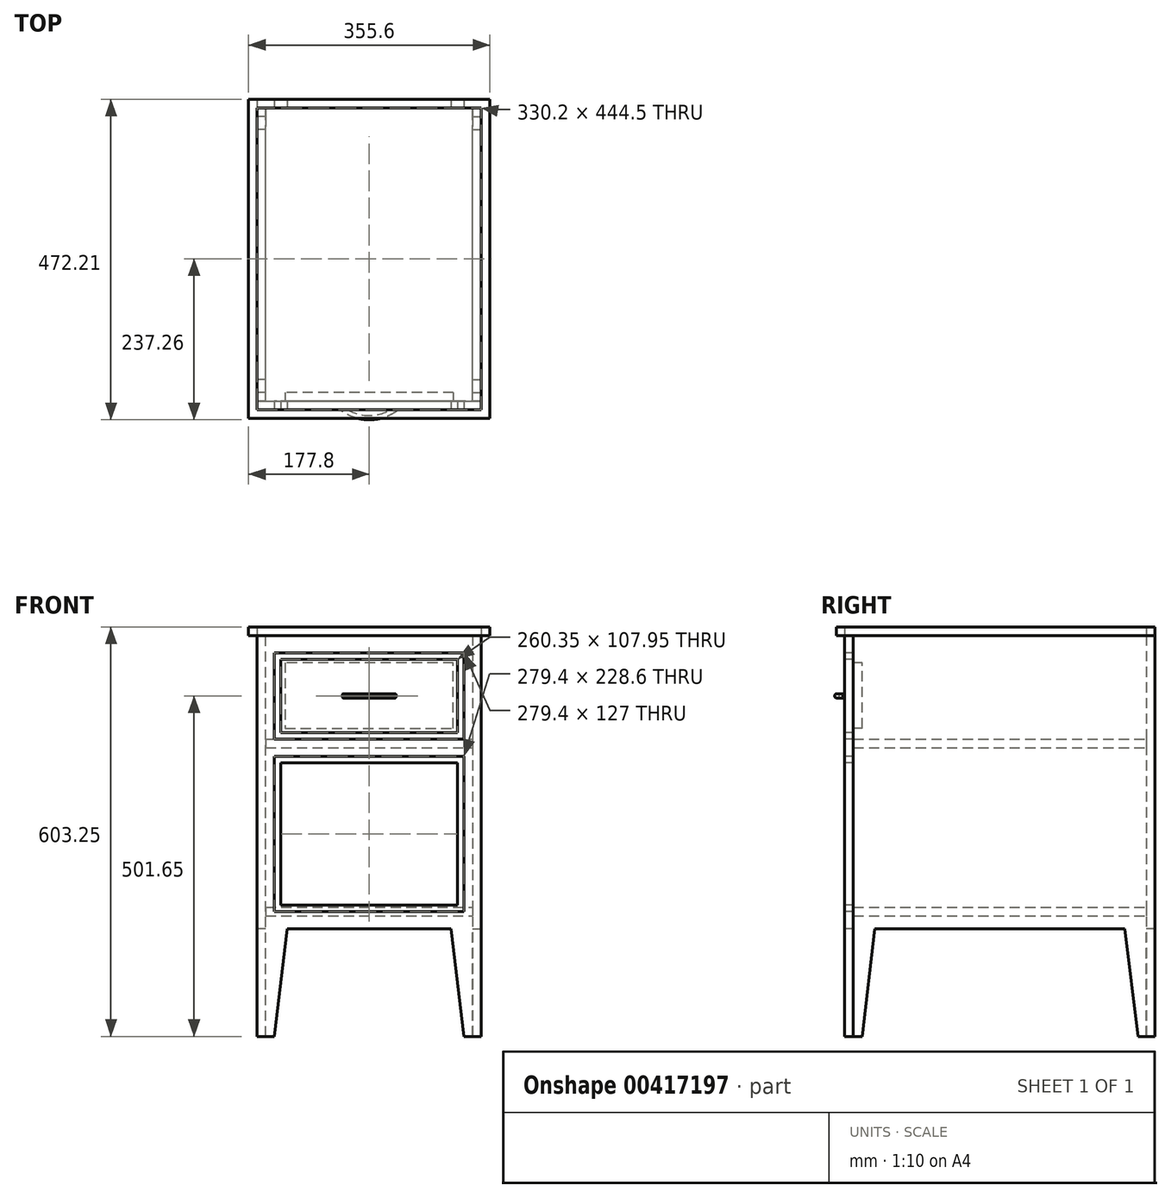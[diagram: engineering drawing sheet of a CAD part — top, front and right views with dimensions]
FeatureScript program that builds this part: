
annotation { "Feature Type Name" : "Feature", "Feature Type Description" : "" }
export const myFeature = defineFeature(function(context is Context, id is Id, definition is map)
    precondition{}
    {
        {
            var Q0;
            Q0=qCreatedBy(makeId("Front.planeOp"),FACE);
            var sketch = newSketch(context, id + "F0", { "sketchPlane" : qUnion([Q0])});
            skLineSegment(sketch, "E0.bottom", {"start": v(44.45, 0) * mm, "end": v(285.75, 0) * mm});
            skLineSegment(sketch, "E0.top", {"start": v(0, 431.8) * mm, "end": v(330.2, 431.8) * mm});
            skLineSegment(sketch, "E0.left", {"start": v(0, 0) * mm, "end": v(0, 431.8) * mm});
            skLineSegment(sketch, "E0.right", {"start": v(330.2, 0) * mm, "end": v(330.2, 431.8) * mm});
            skLineSegment(sketch, "E1", {"start": v(0, 0) * mm, "end": v(0, -158.75) * mm});
            skLineSegment(sketch, "E2", {"start": v(25.4, -158.75) * mm, "end": v(44.45, 0) * mm});
            skLineSegment(sketch, "E3", {"start": v(0, -158.75) * mm, "end": v(25.4, -158.75) * mm});
            skLineSegment(sketch, "E4", {"start": v(165.1, 431.8) * mm, "end": v(165.1, -6.98) * mm, "construction": true});
            skLineSegment(sketch, "E5.MirrorCS", {"start": v(304.8, -158.75) * mm, "end": v(285.75, 0) * mm});
            skLineSegment(sketch, "E6.MirrorCS", {"start": v(330.2, -158.75) * mm, "end": v(304.8, -158.75) * mm});
            skLineSegment(sketch, "E7.MirrorCS", {"start": v(330.2, 0) * mm, "end": v(330.2, -158.75) * mm});
            skLineSegment(sketch, "E8.bottom", {"start": v(304.8, 279.4) * mm, "end": v(25.4, 279.4) * mm});
            skLineSegment(sketch, "E8.top", {"start": v(304.8, 406.4) * mm, "end": v(25.4, 406.4) * mm});
            skLineSegment(sketch, "E8.left", {"start": v(304.8, 279.4) * mm, "end": v(304.8, 406.4) * mm});
            skLineSegment(sketch, "E8.right", {"start": v(25.4, 279.4) * mm, "end": v(25.4, 406.4) * mm});
            skPoint(sketch, "E8.middle", {"position": v(165.1, 342.9) * mm});
            skLineSegment(sketch, "E9.bottom", {"start": v(304.8, 25.4) * mm, "end": v(25.4, 25.4) * mm});
            skLineSegment(sketch, "E9.top", {"start": v(304.8, 254) * mm, "end": v(25.4, 254) * mm});
            skLineSegment(sketch, "E9.left", {"start": v(304.8, 25.4) * mm, "end": v(304.8, 254) * mm});
            skLineSegment(sketch, "E9.right", {"start": v(25.4, 25.4) * mm, "end": v(25.4, 254) * mm});
            skPoint(sketch, "E9.middle", {"position": v(165.1, 139.7) * mm});
            skSolve(sketch);
        }
        {
            var Q0;
            Q0=makeQuery(id+"F0.imprint","IMPRINT",FACE,{"disambiguationData":[TD([[makeQuery(id+"F0.imprint","IMPRINT",EDGE,{"derivedFrom":sQuery(id+"F0.wireOp",EDGE,"E0.bottom")}),1.0]])]});
            extrude(context, id + "F1", {"entities" : qUnion([Q0]), "oppositeDirection" : true, "depth" : 12.7 * mm});
        }
        {
            var Q0;
            Q0=makeQuery(id+"F1.opExtrude","SWEPT_FACE",FACE,{"disambiguationData":[OSD([sQuery(id+"F0.wireOp",EDGE,"E0.right"),sQuery(id+"F0.wireOp",EDGE,"E7.MirrorCS")])]});
            var sketch = newSketch(context, id + "F2", { "sketchPlane" : qUnion([Q0])});
            skLineSegment(sketch, "E10.0", {"start": v(12.7, 431.8) * mm, "end": v(12.7, -158.75) * mm});
            skLineSegment(sketch, "E11.top", {"start": v(12.7, 431.8) * mm, "end": v(444.5, 431.8) * mm});
            skLineSegment(sketch, "E12", {"start": v(25.4, -158.75) * mm, "end": v(44.45, 0) * mm});
            skLineSegment(sketch, "E13", {"start": v(12.7, -158.75) * mm, "end": v(25.4, -158.75) * mm});
            skLineSegment(sketch, "E14.MirrorCS", {"start": v(431.8, -158.75) * mm, "end": v(412.75, 0) * mm});
            skLineSegment(sketch, "E15.MirrorCS", {"start": v(444.5, -158.75) * mm, "end": v(431.8, -158.75) * mm});
            skLineSegment(sketch, "E16.MirrorCS", {"start": v(444.5, 431.8) * mm, "end": v(444.5, -158.75) * mm});
            skPoint(sketch, "E17.middle", {"position": v(184.15, 419.1) * mm});
            skPoint(sketch, "E18.middle", {"position": v(184.15, 177.8) * mm});
            skLineSegment(sketch, "E19", {"start": v(44.45, 0) * mm, "end": v(412.75, 0) * mm});
            skSolve(sketch);
        }
        {
            var Q0;
            Q0=makeQuery(id+"F2.imprint","IMPRINT",FACE,{"disambiguationData":[TD([[makeQuery(id+"F2.imprint","IMPRINT",EDGE,{"derivedFrom":sQuery(id+"F2.wireOp",EDGE,"E11.top")}),-1.0]])]});
            extrude(context, id + "F3", {"entities" : qUnion([Q0]), "oppositeDirection" : true, "depth" : 12.7 * mm});
        }
        {
            var Q0;
            Q0=makeQuery(id+"F3.opExtrude","SWEPT_FACE",FACE,{"disambiguationData":[OSD([sQuery(id+"F2.wireOp",EDGE,"E16.MirrorCS")])]});
            var sketch = newSketch(context, id + "F4", { "sketchPlane" : qUnion([Q0])});
            skLineSegment(sketch, "E20.bottom", {"start": v(-285.75, 0) * mm, "end": v(-44.45, 0) * mm});
            skLineSegment(sketch, "E20.top", {"start": v(-330.2, 431.8) * mm, "end": v(0, 431.8) * mm});
            skLineSegment(sketch, "E20.left", {"start": v(-330.2, 0) * mm, "end": v(-330.2, 431.8) * mm});
            skLineSegment(sketch, "E20.right", {"start": v(0, 0) * mm, "end": v(0, 431.8) * mm});
            skLineSegment(sketch, "E21", {"start": v(-330.2, 0) * mm, "end": v(-330.2, -158.75) * mm});
            skLineSegment(sketch, "E22", {"start": v(-304.8, -158.75) * mm, "end": v(-285.75, 0) * mm});
            skLineSegment(sketch, "E23", {"start": v(-330.2, -158.75) * mm, "end": v(-304.8, -158.75) * mm});
            skLineSegment(sketch, "E24", {"start": v(-165.1, 431.8) * mm, "end": v(-165.1, 33.68) * mm, "construction": true});
            skLineSegment(sketch, "E25.MirrorCS", {"start": v(-25.4, -158.75) * mm, "end": v(-44.45, 0) * mm});
            skLineSegment(sketch, "E26.MirrorCS", {"start": v(0, -158.75) * mm, "end": v(-25.4, -158.75) * mm});
            skLineSegment(sketch, "E27.MirrorCS", {"start": v(0, 0) * mm, "end": v(0, -158.75) * mm});
            skPoint(sketch, "E28.middle", {"position": v(-165.1, 419.1) * mm});
            skPoint(sketch, "E29.middle", {"position": v(-165.1, 177.8) * mm});
            skSolve(sketch);
        }
        {
            var Q0;
            Q0=qSketchRegion(id+"F4",true);
            extrude(context, id + "F5", {"entities" : qUnion([Q0]), "operationType" : NewBodyOperationType.ADD, "depth" : 12.7 * mm});
        }
        {
            var Q0;
            Q0=qCreatedBy(makeId("Right.planeOp"),FACE);
            var sketch = newSketch(context, id + "F6", { "sketchPlane" : qUnion([Q0])});
            skLineSegment(sketch, "E30.0", {"start": v(25.4, -158.75) * mm, "end": v(44.45, 0) * mm});
            skLineSegment(sketch, "E31.0", {"start": v(44.45, 0) * mm, "end": v(412.75, 0) * mm});
            skLineSegment(sketch, "E32.0", {"start": v(431.8, -158.75) * mm, "end": v(412.75, 0) * mm});
            skLineSegment(sketch, "E33.0", {"start": v(12.7, -158.75) * mm, "end": v(12.7, 431.8) * mm});
            skLineSegment(sketch, "E34.0", {"start": v(444.5, 431.8) * mm, "end": v(444.5, -158.75) * mm});
            skLineSegment(sketch, "E35.0", {"start": v(12.7, 431.8) * mm, "end": v(444.5, 431.8) * mm});
            skLineSegment(sketch, "E36.0", {"start": v(12.7, -158.75) * mm, "end": v(25.4, -158.75) * mm});
            skLineSegment(sketch, "E37.0", {"start": v(444.5, -158.75) * mm, "end": v(431.8, -158.75) * mm});
            skSolve(sketch);
        }
        {
            var Q0;
            Q0=qSketchRegion(id+"F6",true);
            extrude(context, id + "F7", {"entities" : qUnion([Q0]), "depth" : 12.7 * mm});
        }
        {
            var Q0;
            Q0=makeQuery(id+"F7.boolean.opBoolean","MERGE",FACE,{"derivedFrom":[makeQuery(id+"F5.boolean.opBoolean","MERGE",FACE,{"derivedFrom":[makeQuery(id+"F3.boolean.opBoolean","MERGE",FACE,{"derivedFrom":[makeQuery(id+"F1.opExtrude","SWEPT_FACE",FACE,{"disambiguationData":[OSD([sQuery(id+"F0.wireOp",EDGE,"E0.top")])]}),makeQuery(id+"F3.opExtrude","SWEPT_FACE",FACE,{"disambiguationData":[OSD([sQuery(id+"F2.wireOp",EDGE,"E11.top")])]})]}),makeQuery(id+"F5.opExtrude","SWEPT_FACE",FACE,{"disambiguationData":[OSD([sQuery(id+"F4.wireOp",EDGE,"E20.top")])]})]}),makeQuery(id+"F7.opExtrude","SWEPT_FACE",FACE,{"disambiguationData":[OSD([sQuery(id+"F6.wireOp",EDGE,"E35.0")])]})]});
            var sketch = newSketch(context, id + "F8", { "sketchPlane" : qUnion([Q0])});
            skLineSegment(sketch, "E38", {"start": v(165.1, 12.7) * mm, "end": v(165.1, 444.5) * mm, "construction": true});
            skLineSegment(sketch, "E39.top", {"start": v(330.2, 0) * mm, "end": v(0, 0) * mm});
            skLineSegment(sketch, "E39.left", {"start": v(330.2, 444.5) * mm, "end": v(330.2, 0) * mm});
            skLineSegment(sketch, "E39.right", {"start": v(0, 444.5) * mm, "end": v(0, 0) * mm});
            skPoint(sketch, "E40", {"position": v(165.1, 228.6) * mm});
            skLineSegment(sketch, "E41", {"start": v(0, 444.5) * mm, "end": v(330.2, 444.5) * mm});
            skSolve(sketch);
        }
        {
            var Q0;
            Q0=qSketchRegion(id+"F8",true);
            extrude(context, id + "F9", {"entities" : qUnion([Q0]), "depth" : 12.7 * mm});
        }
        {
            var Q0;
            Q0=makeQuery(id+"F0.imprint","IMPRINT",FACE,{"disambiguationData":[TD([[makeQuery(id+"F0.imprint","IMPRINT",EDGE,{"derivedFrom":sQuery(id+"F0.wireOp",EDGE,"E0.bottom")}),1.0]])]});
            var sketch = newSketch(context, id + "F10", { "sketchPlane" : qUnion([Q0])});
            skLineSegment(sketch, "E42.0.0", {"start": v(304.8, 279.4) * mm, "end": v(304.8, 406.4) * mm});
            skLineSegment(sketch, "E42.0.1", {"start": v(304.8, 406.4) * mm, "end": v(25.4, 406.4) * mm});
            skLineSegment(sketch, "E42.0.2", {"start": v(25.4, 406.4) * mm, "end": v(25.4, 279.4) * mm});
            skLineSegment(sketch, "E42.0.3", {"start": v(25.4, 279.4) * mm, "end": v(304.8, 279.4) * mm});
            skLineSegment(sketch, "E43.0", {"start": v(34.93, 288.93) * mm, "end": v(295.28, 288.93) * mm});
            skLineSegment(sketch, "E43.1", {"start": v(34.93, 396.88) * mm, "end": v(34.93, 288.93) * mm});
            skLineSegment(sketch, "E43.2", {"start": v(295.28, 396.88) * mm, "end": v(34.93, 396.88) * mm});
            skLineSegment(sketch, "E43.3", {"start": v(295.28, 288.93) * mm, "end": v(295.28, 396.88) * mm});
            skSolve(sketch);
        }
        {
            var Q0;
            Q0=makeQuery(id+"F10.imprint","IMPRINT",FACE,{"disambiguationData":[TD([[makeQuery(id+"F10.imprint","IMPRINT",EDGE,{"derivedFrom":sQuery(id+"F10.wireOp",EDGE,"E43.0")}),1.0]])]});
            extrude(context, id + "F11", {"entities" : qUnion([Q0]), "oppositeDirection" : true, "depth" : 12.7 * mm});
        }
        {
            var Q0;
            Q0=makeQuery(id+"F7.opExtrude","SWEPT_FACE",FACE,{"disambiguationData":[OSD([sQuery(id+"F6.wireOp",EDGE,"E31.0")])]});
            var sketch = newSketch(context, id + "F12", { "sketchPlane" : qUnion([Q0])});
            skLineSegment(sketch, "E44.0", {"start": v(12.7, -12.7) * mm, "end": v(317.5, -12.7) * mm});
            skLineSegment(sketch, "E44.1", {"start": v(12.7, -12.7) * mm, "end": v(12.7, -444.5) * mm});
            skPoint(sketch, "E45.orphan", {"position": v(12.7, -44.45) * mm});
            skPoint(sketch, "E46.orphan", {"position": v(44.45, -12.7) * mm});
            skLineSegment(sketch, "E47.0", {"start": v(317.5, -12.7) * mm, "end": v(317.5, -444.5) * mm});
            skPoint(sketch, "E48.orphan", {"position": v(285.75, -12.7) * mm});
            skPoint(sketch, "E49.orphan", {"position": v(317.5, -44.45) * mm});
            skLineSegment(sketch, "E50.0", {"start": v(317.5, -444.5) * mm, "end": v(12.7, -444.5) * mm});
            skPoint(sketch, "E51.orphan", {"position": v(317.5, -412.75) * mm});
            skPoint(sketch, "E52.orphan", {"position": v(285.75, -444.5) * mm});
            skPoint(sketch, "E53.orphan", {"position": v(44.45, -444.5) * mm});
            skPoint(sketch, "E54.orphan", {"position": v(12.7, -412.75) * mm});
            skSolve(sketch);
        }
        {
            var Q0;
            Q0=qSketchRegion(id+"F12",true);
            extrude(context, id + "F13", {"entities" : qUnion([Q0]), "oppositeDirection" : true, "depth" : 12.7 * mm});
        }
        {
            var Q0;
            Q0=makeQuery(id+"F13.opExtrude","SWEPT_BODY",BODY,{"disambiguationData":[OSD([sQuery(id+"F12.wireOp",EDGE,"E44.0"),sQuery(id+"F12.wireOp",EDGE,"E44.1"),sQuery(id+"F12.wireOp",EDGE,"E47.0"),sQuery(id+"F12.wireOp",EDGE,"E50.0")])]});
            transform(context, id + "F14", {"entities" : qUnion([Q0]), "transformType" : TransformType.TRANSLATION_3D, "dx" : 0 * mm, "dy" : 0 * mm, "dz" : 12.7 * mm, "makeCopy" : true});
        }
        {
            var Q0;
            Q0=makeQuery(id+"F14.opPattern","COPY",BODY,{"derivedFrom":makeQuery(id+"F13.opExtrude","SWEPT_BODY",BODY,{"disambiguationData":[OSD([sQuery(id+"F12.wireOp",EDGE,"E44.0"),sQuery(id+"F12.wireOp",EDGE,"E44.1"),sQuery(id+"F12.wireOp",EDGE,"E47.0"),sQuery(id+"F12.wireOp",EDGE,"E50.0")])]}),"instanceName":"1"});
            transform(context, id + "F15", {"entities" : qUnion([Q0]), "transformType" : TransformType.TRANSLATION_3D, "dx" : 0 * mm, "dy" : 0 * mm, "dz" : 254 * mm, "makeCopy" : true});
        }
        {
            var Q0;
            Q0=makeQuery(id+"F11.opExtrude","CAP_FACE",FACE,{"disambiguationData":[OSD([sQuery(id+"F10.wireOp",EDGE,"E43.0"),sQuery(id+"F10.wireOp",EDGE,"E43.1"),sQuery(id+"F10.wireOp",EDGE,"E43.2"),sQuery(id+"F10.wireOp",EDGE,"E43.3")])],"isStart":false});
            var sketch = newSketch(context, id + "F16", { "sketchPlane" : qUnion([Q0])});
            skLineSegment(sketch, "E55.0", {"start": v(-288.93, 391.8) * mm, "end": v(-41.28, 391.8) * mm});
            skLineSegment(sketch, "E56.0", {"start": v(-288.93, 295.28) * mm, "end": v(-288.93, 391.8) * mm});
            skLineSegment(sketch, "E56.1", {"start": v(-41.28, 295.28) * mm, "end": v(-288.93, 295.28) * mm});
            skLineSegment(sketch, "E56.2", {"start": v(-41.28, 391.8) * mm, "end": v(-41.28, 295.28) * mm});
            skSolve(sketch);
        }
        {
            var Q0;
            Q0 = qSketchRegion(id + "F16", true);
            extrude(context, id + "F17", {"entities" : qUnion([Q0]), "depth" : 12.7 * mm});
        }
        {
            var Q0;
            Q0=makeQuery(id+"F13.opExtrude","SWEPT_BODY",BODY,{"disambiguationData":[OSD([sQuery(id+"F12.wireOp",EDGE,"E44.0"),sQuery(id+"F12.wireOp",EDGE,"E44.1"),sQuery(id+"F12.wireOp",EDGE,"E47.0"),sQuery(id+"F12.wireOp",EDGE,"E50.0")])]});
            deleteBodies(context, id + "F18", {"entities" : qUnion([Q0])});
        }
        {
            var Q0;
            Q0=makeQuery(id+"F1.opExtrude","CAP_FACE",FACE,{"disambiguationData":[OSD([sQuery(id+"F0.wireOp",EDGE,"E0.bottom"),sQuery(id+"F0.wireOp",EDGE,"E0.top"),sQuery(id+"F0.wireOp",EDGE,"E0.left"),sQuery(id+"F0.wireOp",EDGE,"E0.right"),sQuery(id+"F0.wireOp",EDGE,"E1"),sQuery(id+"F0.wireOp",EDGE,"E2"),sQuery(id+"F0.wireOp",EDGE,"E3"),sQuery(id+"F0.wireOp",EDGE,"E5.MirrorCS"),sQuery(id+"F0.wireOp",EDGE,"E6.MirrorCS"),sQuery(id+"F0.wireOp",EDGE,"E7.MirrorCS"),sQuery(id+"F0.wireOp",EDGE,"E8.bottom"),sQuery(id+"F0.wireOp",EDGE,"E8.top"),sQuery(id+"F0.wireOp",EDGE,"E8.left"),sQuery(id+"F0.wireOp",EDGE,"E8.right"),sQuery(id+"F0.wireOp",EDGE,"E9.bottom"),sQuery(id+"F0.wireOp",EDGE,"E9.top"),sQuery(id+"F0.wireOp",EDGE,"E9.left"),sQuery(id+"F0.wireOp",EDGE,"E9.right")])],"isStart":true});
            var sketch = newSketch(context, id + "F19", { "sketchPlane" : qUnion([Q0])});
            skLineSegment(sketch, "E57.0", {"start": v(25.4, 279.4) * mm, "end": v(25.4, 406.4) * mm});
            skLineSegment(sketch, "E57.1", {"start": v(304.8, 406.4) * mm, "end": v(25.4, 406.4) * mm});
            skLineSegment(sketch, "E57.2", {"start": v(304.8, 279.4) * mm, "end": v(304.8, 406.4) * mm});
            skLineSegment(sketch, "E57.3", {"start": v(304.8, 279.4) * mm, "end": v(25.4, 279.4) * mm});
            skLineSegment(sketch, "E58.0", {"start": v(295.28, 396.88) * mm, "end": v(34.93, 396.88) * mm});
            skLineSegment(sketch, "E58.1", {"start": v(295.28, 288.93) * mm, "end": v(295.28, 396.88) * mm});
            skLineSegment(sketch, "E58.2", {"start": v(295.28, 288.93) * mm, "end": v(34.93, 288.93) * mm});
            skLineSegment(sketch, "E58.3", {"start": v(34.93, 288.93) * mm, "end": v(34.93, 396.88) * mm});
            skSolve(sketch);
        }
        {
            var Q0;
            Q0 = qSketchRegion(id + "F19", true);
            extrude(context, id + "F20", {"entities" : qUnion([Q0]), "oppositeDirection" : true, "depth" : 12.7 * mm});
        }
        {
            var Q0;
            Q0=makeQuery(id+"F1.opExtrude","CAP_FACE",FACE,{"disambiguationData":[OSD([sQuery(id+"F0.wireOp",EDGE,"E0.bottom"),sQuery(id+"F0.wireOp",EDGE,"E0.top"),sQuery(id+"F0.wireOp",EDGE,"E0.left"),sQuery(id+"F0.wireOp",EDGE,"E0.right"),sQuery(id+"F0.wireOp",EDGE,"E1"),sQuery(id+"F0.wireOp",EDGE,"E2"),sQuery(id+"F0.wireOp",EDGE,"E3"),sQuery(id+"F0.wireOp",EDGE,"E5.MirrorCS"),sQuery(id+"F0.wireOp",EDGE,"E6.MirrorCS"),sQuery(id+"F0.wireOp",EDGE,"E7.MirrorCS"),sQuery(id+"F0.wireOp",EDGE,"E8.bottom"),sQuery(id+"F0.wireOp",EDGE,"E8.top"),sQuery(id+"F0.wireOp",EDGE,"E8.left"),sQuery(id+"F0.wireOp",EDGE,"E8.right"),sQuery(id+"F0.wireOp",EDGE,"E9.bottom"),sQuery(id+"F0.wireOp",EDGE,"E9.top"),sQuery(id+"F0.wireOp",EDGE,"E9.left"),sQuery(id+"F0.wireOp",EDGE,"E9.right")])],"isStart":true});
            var sketch = newSketch(context, id + "F21", { "sketchPlane" : qUnion([Q0])});
            skLineSegment(sketch, "E59.0", {"start": v(304.8, 254) * mm, "end": v(25.4, 254) * mm});
            skLineSegment(sketch, "E59.1", {"start": v(25.4, 25.4) * mm, "end": v(25.4, 254) * mm});
            skLineSegment(sketch, "E59.2", {"start": v(304.8, 25.4) * mm, "end": v(25.4, 25.4) * mm});
            skLineSegment(sketch, "E59.3", {"start": v(304.8, 25.4) * mm, "end": v(304.8, 254) * mm});
            skLineSegment(sketch, "E60.0", {"start": v(295.28, 244.47) * mm, "end": v(34.93, 244.47) * mm});
            skLineSegment(sketch, "E60.1", {"start": v(295.28, 34.93) * mm, "end": v(295.28, 244.47) * mm});
            skLineSegment(sketch, "E60.2", {"start": v(295.28, 34.93) * mm, "end": v(34.93, 34.93) * mm});
            skLineSegment(sketch, "E60.3", {"start": v(34.93, 34.93) * mm, "end": v(34.93, 244.47) * mm});
            skSolve(sketch);
        }
        {
            var Q0;
            Q0 = qSketchRegion(id + "F21", true);
            extrude(context, id + "F22", {"entities" : qUnion([Q0]), "oppositeDirection" : true, "depth" : 12.7 * mm});
        }
        {
            var Q0;
            Q0=makeQuery(id+"F9.opExtrude","SWEPT_EDGE",EDGE,{"disambiguationData":[OSD([sQuery(id+"F8.wireOp",EDGE,"E39.top"),sQuery(id+"F8.wireOp",EDGE,"E39.left")])]});
            cPoint(context, id + "F23", {"entities" : qUnion([Q0]), "parameter" : 0.5});
        }
        {
            var Q0;
            Q0=makeQuery(id+"F14.opPattern","COPY",BODY,{"derivedFrom":makeQuery(id+"F13.opExtrude","SWEPT_BODY",BODY,{"disambiguationData":[OSD([sQuery(id+"F12.wireOp",EDGE,"E44.0"),sQuery(id+"F12.wireOp",EDGE,"E44.1"),sQuery(id+"F12.wireOp",EDGE,"E47.0"),sQuery(id+"F12.wireOp",EDGE,"E50.0")])]}),"instanceName":"1"});
            var Q1;
            Q1=makeQuery(id+"F9.opExtrude","CAP_VERTEX",VERTEX,{"disambiguationData":[OSD([sQuery(id+"F8.wireOp",EDGE,"E39.top"),sQuery(id+"F8.wireOp",EDGE,"E39.left")])],"isStart":true});
            var Q2;
            Q2 = qCreatedBy(id + "F23" ,VERTEX);
            transform(context, id + "F24", {"entities" : qUnion([Q0]), "transformType" : TransformType.TRANSLATION_ENTITY, "oppositeDirectionEntity" : false, "transformLine" : qUnion([Q1, Q2]), "makeCopy" : false});
        }
        {
            var Q0;
            Q0=makeQuery(id+"F11.opExtrude","CAP_FACE",FACE,{"disambiguationData":[OSD([sQuery(id+"F10.wireOp",EDGE,"E43.0"),sQuery(id+"F10.wireOp",EDGE,"E43.1"),sQuery(id+"F10.wireOp",EDGE,"E43.2"),sQuery(id+"F10.wireOp",EDGE,"E43.3")])],"isStart":true});
            var sketch = newSketch(context, id + "F25", { "sketchPlane" : qUnion([Q0])});
            skLineSegment(sketch, "E61", {"start": v(34.93, 342.9) * mm, "end": v(295.28, 342.9) * mm, "construction": true});
            skLineSegment(sketch, "E62", {"start": v(165.1, 342.9) * mm, "end": v(165.1, 396.88) * mm, "construction": true});
            skSolve(sketch);
        }
        {
            var Q0;
            Q0=makeQuery(id+"F11.opExtrude","CAP_EDGE",EDGE,{"disambiguationData":[OSD([sQuery(id+"F10.wireOp",EDGE,"E43.1")])],"isStart":true});
            cPlane(context, id + "F26", {"entities" : qUnion([Q0]), "cplaneType" : CPlaneType.MID_PLANE, "offset" : 25.4 * mm, "width" : 152.4 * mm, "height" : 152.4 * mm});
        }
        {
            var Q0;
            Q0=qCreatedBy(id+"F26.planeOp",FACE);
            var sketch = newSketch(context, id + "F27", { "sketchPlane" : qUnion([Q0])});
            skPoint(sketch, "E63", {"position": v(127, 0) * mm});
            skArc(sketch, "E64", {"start": v(203.2, 0) * mm, "mid": v(165.1, 11.84) * mm, "end": v(127, 0) * mm});
            skSolve(sketch);
        }
        {
            var Q0;
            Q0=makeQuery(id+"F11.opExtrude","CAP_EDGE",EDGE,{"disambiguationData":[OSD([sQuery(id+"F10.wireOp",EDGE,"E43.2")])],"isStart":true});
            cPlane(context, id + "F28", {"entities" : qUnion([Q0]), "cplaneType" : CPlaneType.MID_PLANE, "offset" : 25.4 * mm, "width" : 152.4 * mm, "height" : 152.4 * mm});
        }
        {
            var Q0;
            Q0=qCreatedBy(id+"F28.planeOp",FACE);
            var sketch = newSketch(context, id + "F29", { "sketchPlane" : qUnion([Q0])});
            skCircle(sketch, "E65", {"center": v(11.84, 342.9) * mm, "radius": 3.18 * mm});
            skSolve(sketch);
        }
        {
            var Q0;
            Q0=makeQuery(id+"F29.imprint","IMPRINT",FACE,{"disambiguationData":[TD([[makeQuery(id+"F29.imprint","IMPRINT",EDGE,{"derivedFrom":sQuery(id+"F29.wireOp",EDGE,"E65")}),1.0]])]});
            var Q1;
            Q1=sQuery(id+"F27.wireOp",EDGE,"E64");
            sweep(context, id + "F30", {"profiles" : qUnion([Q0]), "path" : qUnion([Q1])});
        }
        {
            var Q0;
            Q0=makeQuery(id+"F30.opSweep","SWEPT_BODY",BODY,{"disambiguationData":[OSD([sQuery(id+"F27.wireOp",EDGE,"E64"),sQuery(id+"F29.wireOp",EDGE,"E65")])]});
            var Q1;
            Q1=qCreatedBy(id+"F28.planeOp",FACE);
            mirror(context, id + "F31", {"entities" : qUnion([Q0]), "mirrorPlane" : qUnion([Q1])});
        }
        {
            var Q0;
            Q0=makeQuery(id+"F11.opExtrude","SWEPT_BODY",BODY,{"disambiguationData":[OSD([sQuery(id+"F10.wireOp",EDGE,"E43.0"),sQuery(id+"F10.wireOp",EDGE,"E43.1"),sQuery(id+"F10.wireOp",EDGE,"E43.2"),sQuery(id+"F10.wireOp",EDGE,"E43.3")])]});
            var Q1;
            Q1=makeQuery(id+"F30.opSweep","SWEPT_BODY",BODY,{"disambiguationData":[OSD([sQuery(id+"F27.wireOp",EDGE,"E64"),sQuery(id+"F29.wireOp",EDGE,"E65")])]});
            var Q2;
            Q2=makeQuery(id+"F31.opPattern","COPY",BODY,{"derivedFrom":makeQuery(id+"F30.opSweep","SWEPT_BODY",BODY,{"disambiguationData":[OSD([sQuery(id+"F27.wireOp",EDGE,"E64"),sQuery(id+"F29.wireOp",EDGE,"E65")])]}),"instanceName":"1"});
            booleanBodies(context, id + "F32", {"operationType" : BooleanOperationType.SUBTRACTION, "tools" : qUnion([Q0]), "targets" : qUnion([Q1, Q2]), "keepTools" : true});
        }
        {
            var Q0;
            Q0=makeQuery(id+"F9.opExtrude","CAP_FACE",FACE,{"disambiguationData":[OSD([sQuery(id+"F8.wireOp",EDGE,"E39.top"),sQuery(id+"F8.wireOp",EDGE,"E39.left"),sQuery(id+"F8.wireOp",EDGE,"E39.right"),sQuery(id+"F8.wireOp",EDGE,"E41")])],"isStart":false});
            var sketch = newSketch(context, id + "F33", { "sketchPlane" : qUnion([Q0])});
            skLineSegment(sketch, "E66.0", {"start": v(-12.7, -12.7) * mm, "end": v(-12.7, 457.2) * mm});
            skLineSegment(sketch, "E66.1", {"start": v(-12.7, -12.7) * mm, "end": v(342.9, -12.7) * mm});
            skLineSegment(sketch, "E66.2", {"start": v(342.9, -12.7) * mm, "end": v(342.9, 457.2) * mm});
            skLineSegment(sketch, "E66.3", {"start": v(342.9, 457.2) * mm, "end": v(-12.7, 457.2) * mm});
            skSolve(sketch);
        }
        {
            var Q0;
            Q0=makeQuery(id+"F33.imprint","IMPRINT",FACE,{"disambiguationData":[TD([[makeQuery(id+"F33.imprint","IMPRINT",EDGE,{"derivedFrom":sQuery(id+"F33.wireOp",EDGE,"E66.0")}),-1.0]])]});
            extrude(context, id + "F34", {"entities" : qUnion([Q0]), "oppositeDirection" : true, "depth" : 12.7 * mm});
        }
    });
